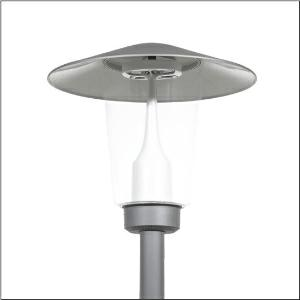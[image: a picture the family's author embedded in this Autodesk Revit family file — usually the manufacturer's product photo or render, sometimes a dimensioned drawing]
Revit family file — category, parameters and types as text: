
# Revit family: pilzleuchte_iq___p1_0a_5xa5235ff14hp_c3dc
name_source: partatom
category: Lighting Fixtures
units: mm (PartAtom-declared; Revit-internal decimal feet)

## family parameters
Cut with Voids When Loaded = No
Host = Face
Light Source = No
Part Type = Normal
Room Calculation Point = No
Round Connector Dimension = Use Diameter
Shared = No

## types (1)
- --- (1 x LED, 4740 lm, 33.6 W, 3000K)
    Apparent Load = 34 VA
    CIE Flux Codes = 35 64 90 96 100
    Color Rendering = 70
    Color Temperature = 3000K
    Default Elevation = 1800 mm
    Description = Mushroom Luminaire iQ, mast luminaire, Module 540 iQ-SR, primary light control with 3 zone facetted reflector, of plastic, silver coated, highly specular, structured, primary optical cover: cover, of PMMA, transparent, light distribution: P1.0a, light emission: direct distribution, primary light characteristic: strongly asymmetric, installation type: post-top, LED, High Power LED, rated luminous flux: 4.740lm, luminous efficacy: 141lm/W, light colour: 730, colour temperature: 3000K, control gear: ECG iQ, control: presetting dimming logarithmic, Street-Remote, Auto-Match, Temp-Guard, Lumen-Switch, Night-Set, Smart-Wire, Light-Fading, Desk-Remote (wireless, voltage-free reading and setting of iQ features in the workshop via application-optimized NFC function/RFID function), optimised constant luminous flux control (CLO 2.0), with terminal, 6-pole, max. 2.5mm², mains connection: 230..240V, AC, 50/60Hz, start of lifetime: 34W, end of service life: 36W, reduction: 15W, luminaire housing, upper part, of glass-fibre reinforced polyester, coated, Siteco® metallic grey (DB 702S), diameter: 650mm, height: 586mm, spigot size: d x l = 76 x 70mm (post-top) | with reducer (optional accessory) 60 x 70mm, post-top mast mounting element, of diecast aluminium, coated, Siteco® metallic grey (DB 702S), Module 540 iQ-SR, traffic white (RAL 9016), equipment: Power, protection rating (complete): IP65, insulation class (complete): insulation class II (safety insulation), certification: CE, ENEC, VDE, packaging unit: 1 piece

Light Distribution: P1.0a
    Height = 586 mm
    Lamp = 1 x LED
    Lamp Light Flux = 4740 lm
    Lamp Power = 33.6 W
    Lamp count = 1
    Length = 650 mm
    Luminous efficacy = 141 lm/W
    Manufacturer = Siteco
    ModVariant = No
    Model = 5XA5235FF14HP
    Number of Poles = 1
    OnlyDefault = Yes
    Power Factor = 1
    Product Name = Pilzleuchte iQ | P1.0a
    Product group = mast luminaire | pylon top
    ProductGroupID = 6100
    Protection Class = Protection class II
    Protection Degree = IP 65
    RLX_Detail_Level = 1
    RLX_Emergency_Light_Flux = 0 lm
    RLX_Emergency_Type = 0
    RLX_Emergency_Type_DB = No
    RlxData = <blob elided: 51829 chars, md5=04a4ec6a>
    Socket = socket
    Standby Power = 0 W
    System Light Flux = 4740 lm
    System Power = 34 W
    Type Comments = factory setting: luminous flux: 100 % | dim-lin: 254 | 695 mA
    Type Image = l_1006077.jpg
    URL = http://relux.com
    VarID = @adj_144773
    Voltage = 0 V
    Weight = 0.00 kg
    Width = 0 mm  [stored 0 ft]

note: [stored X ft] marks values corroborated as IEEE doubles in the binary element streams (Revit-internal decimal feet)

## geometry (parser evidence)
native form markers: Blend x4, Sweep x13
no freeform markers — native parametric forms only
